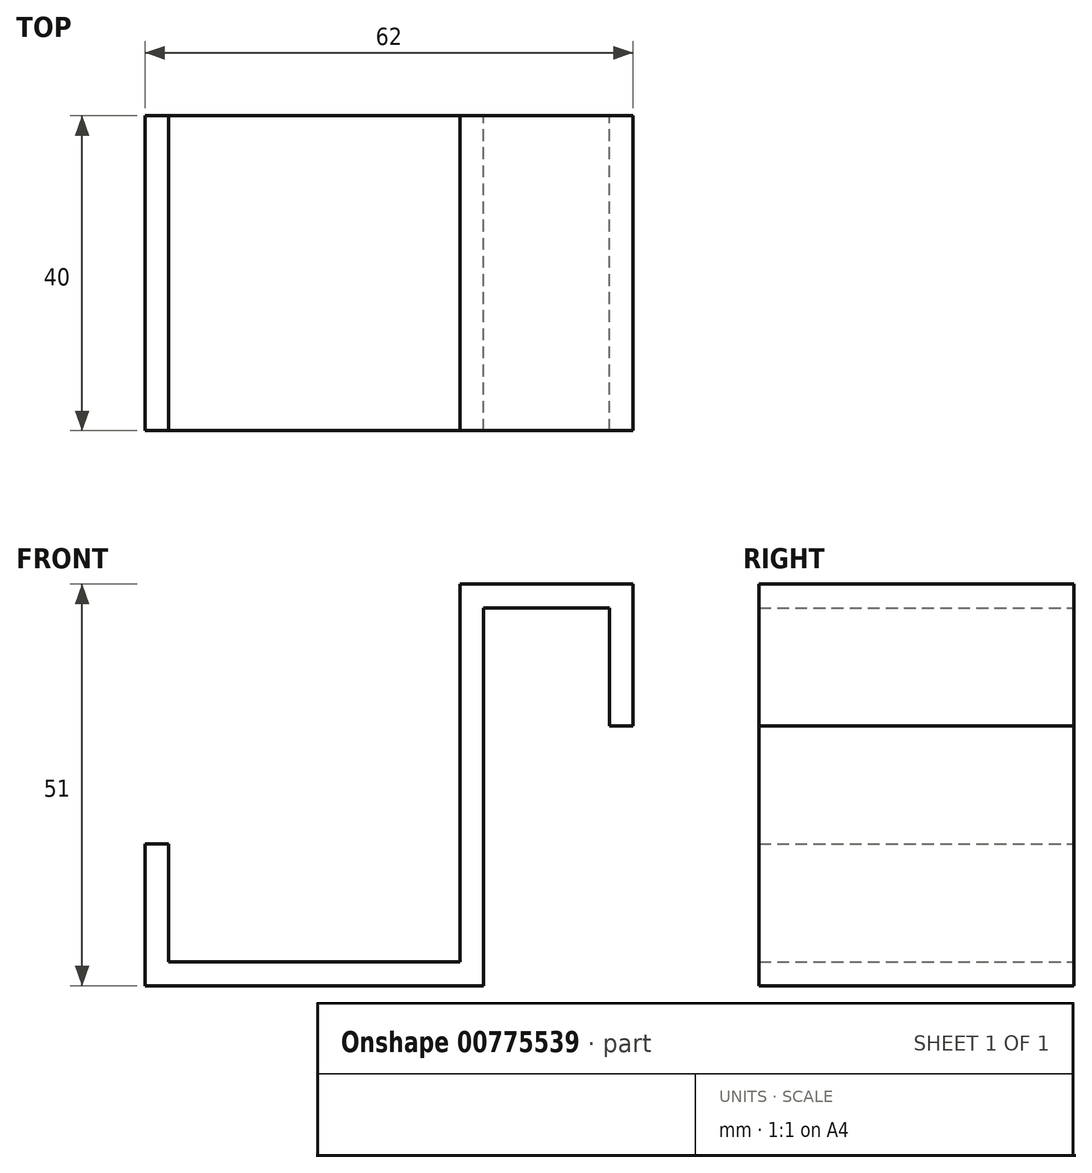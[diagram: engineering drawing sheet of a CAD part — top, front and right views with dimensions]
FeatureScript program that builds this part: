
annotation { "Feature Type Name" : "Feature", "Feature Type Description" : "" }
export const myFeature = defineFeature(function(context is Context, id is Id, definition is map)
    precondition{}
    {
        {
            var Q0;
            Q0=qCreatedBy(makeId("Front.planeOp"),FACE);
            var sketch = newSketch(context, id + "F0", { "sketchPlane" : qUnion([Q0])});
            skLineSegment(sketch, "E0", {"start": v(16, 30) * mm, "end": v(0, 30) * mm});
            skLineSegment(sketch, "E1", {"start": v(0, 30) * mm, "end": v(0, -15) * mm});
            skLineSegment(sketch, "E2", {"start": v(-3, -15) * mm, "end": v(-40, -15) * mm});
            skLineSegment(sketch, "E3", {"start": v(-40, -15) * mm, "end": v(-40, 0) * mm});
            skLineSegment(sketch, "E4", {"start": v(16, 30) * mm, "end": v(16, 15) * mm});
            skLineSegment(sketch, "E5.top", {"start": v(16, 15) * mm, "end": v(19, 15) * mm});
            skLineSegment(sketch, "E5.right", {"start": v(19, 30) * mm, "end": v(19, 15) * mm});
            skLineSegment(sketch, "E6.top", {"start": v(19, 33) * mm, "end": v(0, 33) * mm});
            skLineSegment(sketch, "E6.left", {"start": v(19, 30) * mm, "end": v(19, 33) * mm});
            skLineSegment(sketch, "E7.right", {"start": v(-3, 30) * mm, "end": v(-3, -15) * mm});
            skLineSegment(sketch, "E8.top", {"start": v(0, -18) * mm, "end": v(-43, -18) * mm});
            skLineSegment(sketch, "E8.left", {"start": v(0, -15) * mm, "end": v(0, -18) * mm});
            skLineSegment(sketch, "E9.bottom", {"start": v(-40, 0) * mm, "end": v(-43, 0) * mm});
            skLineSegment(sketch, "E9.top", {"start": v(-40, -18) * mm, "end": v(-43, -18) * mm});
            skLineSegment(sketch, "E9.left", {"start": v(-40, 0) * mm, "end": v(-40, -15) * mm});
            skLineSegment(sketch, "E9.right", {"start": v(-43, 0) * mm, "end": v(-43, -18) * mm});
            skLineSegment(sketch, "E10.bottom", {"start": v(0, 33) * mm, "end": v(-3, 33) * mm});
            skLineSegment(sketch, "E10.right", {"start": v(-3, 33) * mm, "end": v(-3, 30) * mm});
            skSolve(sketch);
        }
        {
            var Q0;
            Q0 = qSketchRegion(id + "F0", true);
            extrude(context, id + "F1", {"entities" : qUnion([Q0]), "depth" : 40 * mm, "offsetDistance" : 25 * mm});
        }
    });
